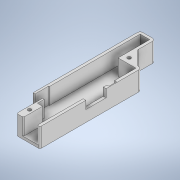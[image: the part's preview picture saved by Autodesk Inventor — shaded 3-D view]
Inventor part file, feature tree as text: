
AUTODESK INVENTOR PART (.ipt)
format: ipt  version: 2021 (Build 250183000, 183)  size: 260,608 bytes
history: native  units: mm
features: sketch x9, extrude x8, fillet x5, hole x2, chamfer x1
ambient origin geometry x8: Origin, YZ Plane, XZ Plane, XY Plane, X Axis, Y Axis, Z Axis, Center Point
bodies: Volumenkörper1 (feature_tree)
feature tree (25):
  sketch  "Skizze1"  dims[d0=20.0mm d1=70.0mm]
  extrude  "Extrusion1"  Depth=70.0mm
  extrude  "Extrusion3"  Depth=23.0mm
  chamfer  "Fase1"  Distance=12.0mm
  fillet  "Rundung1"  Radius=7.0mm
  fillet  "Rundung2"  Radius=2.0mm
  fillet  "Rundung3"  Radius=2.0mm
  fillet  "Rundung4"  Radius=2.0mm
  extrude  "Extrusion4"  Depth=1.0mm
  fillet  "Rundung5"  Radius=14.7mm
  extrude  "Extrusion5"  Depth=5.8mm TaperAngle=0.0deg
  extrude  "Extrusion6"  Depth=1.0mm
  extrude  "Extrusion7"  Depth=3.0mm
  hole  "Bohrung1"  [1 undecoded]
  hole  "Bohrung2"  [1 undecoded]
  extrude  "Extrusion8"  Depth=5.0mm
  extrude  "Extrusion9"  Depth=3.8mm
  sketch  "Skizze4"  dims[d2=7.0mm d3=23.0mm]
  sketch  "Skizze5"  dims[d4=10.0mm]
  sketch  "Skizze6"  dims[d5=14.0mm]
  sketch  "Skizze7"  dims[d6=2.0mm]
  sketch  "Skizze8"  dims[d7=2.0mm]
  sketch  "Skizze9"  dims[d8=2.0mm d9=12.0mm d10=0.0mm d13=7.0mm d14=2.0mm d15=0.0mm]
  sketch  "Skizze10"  dims[d16=10.0mm d17=2.0mm d18=45.0deg d19=2.0mm d20=2.0mm]
  sketch  "Skizze11"  dims[d21=2.0mm d22=1.0mm d24=14.7mm d25=5.8mm d26=0.0mm d27=1.0mm d28=3.0mm d29=0.0mm d30=0.0mm d31=3.0mm d32=0.0mm d34=5.0mm d35=3.8mm d36=3.0mm d37=0.0mm d38=4.0mm d39=4.0mm d40=2.5mm d41=6.0mm d42=4.0mm d43=2.0mm d44=90.0deg d45=8.0mm d46=20.594885mm d47=2.5mm d48=7.0mm d49=2.5mm d50=6.0mm d51=4.0mm d52=2.0mm d53=90.0deg d54=8.0mm d55=20.594885mm d56=23.8mm d58=5.5mm d59=1.5mm d60=15.65mm d61=0.0mm d62=0.0mm d63=0.5mm d64=10.0mm d65=10.0mm d66=0.0mm]
note: 2 required parameter values undecoded (feature->parameter linkage not recoverable at this tier; creation-order binding heuristic only, values carry confidence <= 0.55)
